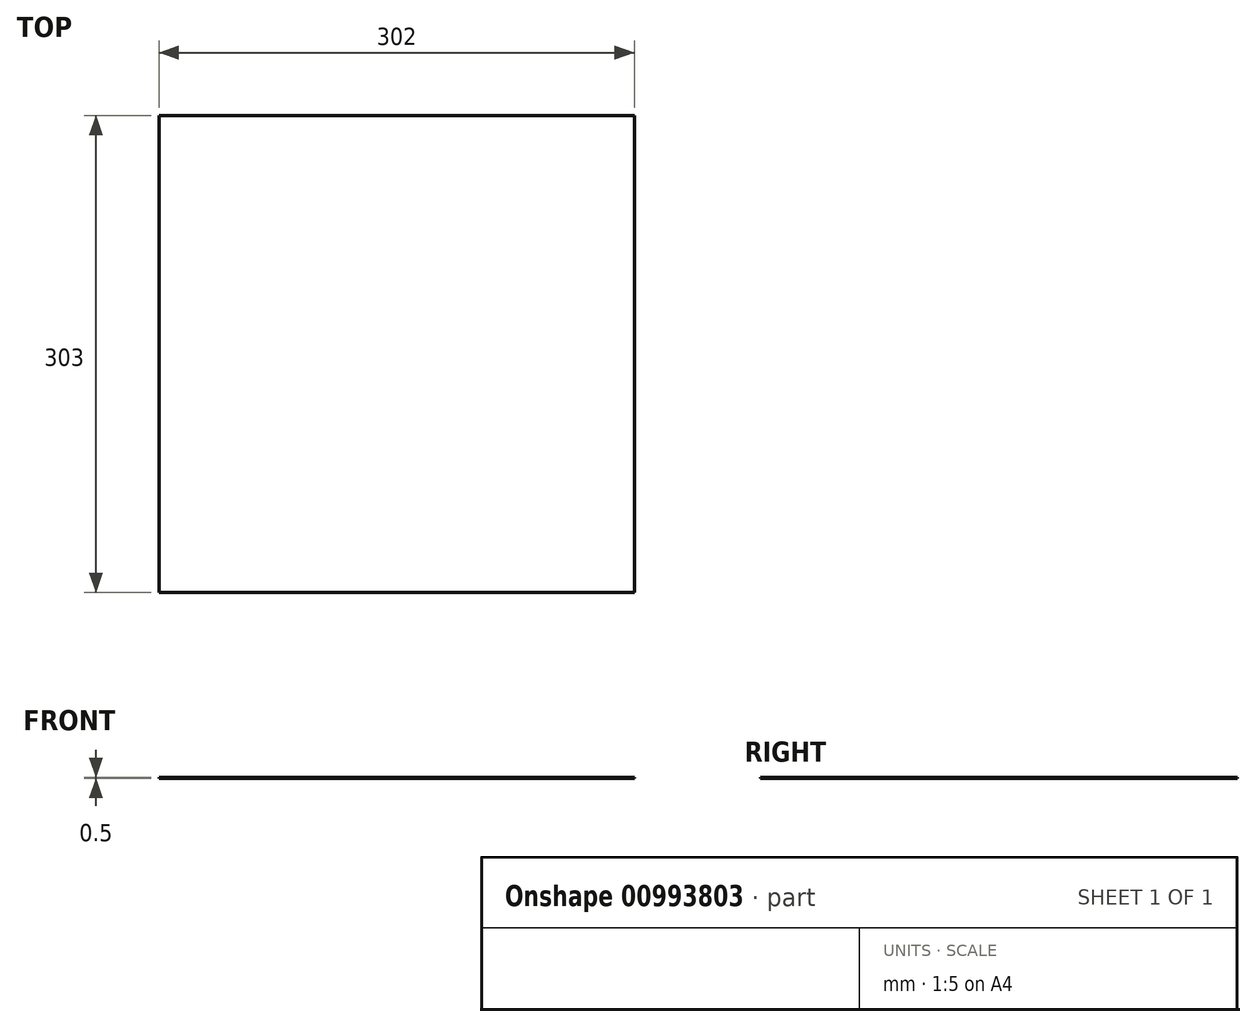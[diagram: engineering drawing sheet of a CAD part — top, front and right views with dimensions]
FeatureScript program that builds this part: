
annotation { "Feature Type Name" : "Feature", "Feature Type Description" : "" }
export const myFeature = defineFeature(function(context is Context, id is Id, definition is map)
    precondition{}
    {
        {
            var Q0;
            Q0=qCreatedBy(makeId("Top.planeOp"),FACE);
            var sketch = newSketch(context, id + "F0", { "sketchPlane" : qUnion([Q0])});
            skLineSegment(sketch, "E0.bottom", {"start": v(151, 151.5) * mm, "end": v(-151, 151.5) * mm});
            skLineSegment(sketch, "E0.top", {"start": v(151, -151.5) * mm, "end": v(-151, -151.5) * mm});
            skLineSegment(sketch, "E0.left", {"start": v(151, 151.5) * mm, "end": v(151, -151.5) * mm});
            skLineSegment(sketch, "E0.right", {"start": v(-151, 151.5) * mm, "end": v(-151, -151.5) * mm});
            skPoint(sketch, "E0.middle", {"position": v(0, 0) * mm});
            skSolve(sketch);
        }
        {
            var Q0;
            Q0=makeQuery(id+"F0.imprint","IMPRINT",FACE,{"disambiguationData":[TD([[makeQuery(id+"F0.imprint","IMPRINT",EDGE,{"derivedFrom":sQuery(id+"F0.wireOp",EDGE,"E0.bottom")}),1.0]])]});
            extrude(context, id + "F1", {"entities" : qUnion([Q0]), "depth" : 0.5 * mm, "offsetDistance" : 25 * mm});
        }
    });
